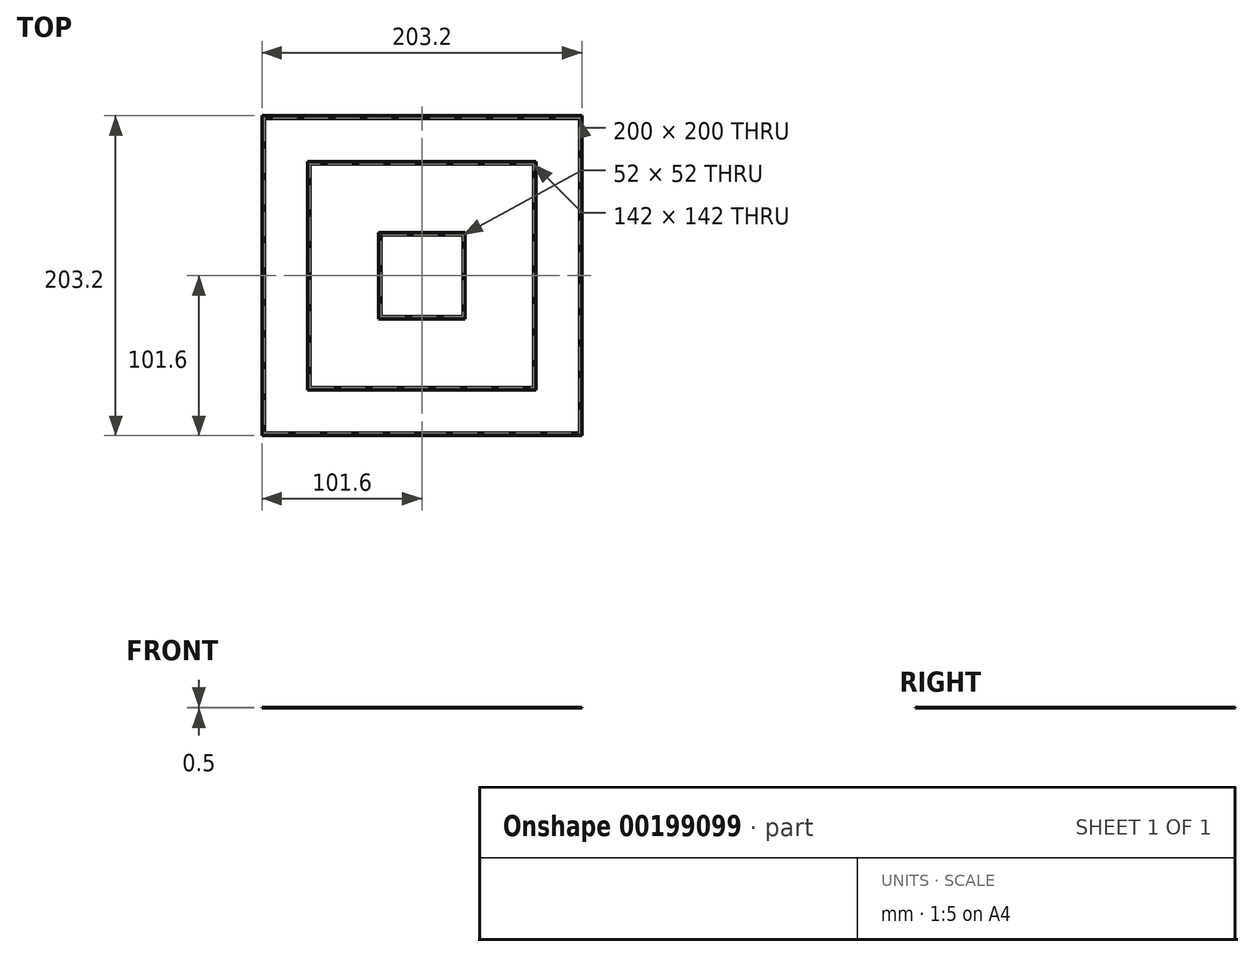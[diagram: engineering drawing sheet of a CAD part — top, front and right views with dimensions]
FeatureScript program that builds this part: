
annotation { "Feature Type Name" : "Feature", "Feature Type Description" : "" }
export const myFeature = defineFeature(function(context is Context, id is Id, definition is map)
    precondition{}
    {
        {
            var Q0;
            Q0=qCreatedBy(makeId("Top.planeOp"),FACE);
            var sketch = newSketch(context, id + "F0", { "sketchPlane" : qUnion([Q0])});
            skLineSegment(sketch, "E0.bottom", {"start": v(101.6, 101.6) * mm, "end": v(-101.6, 101.6) * mm});
            skLineSegment(sketch, "E0.top", {"start": v(101.6, -101.6) * mm, "end": v(-101.6, -101.6) * mm});
            skLineSegment(sketch, "E0.left", {"start": v(101.6, 101.6) * mm, "end": v(101.6, -101.6) * mm});
            skLineSegment(sketch, "E0.right", {"start": v(-101.6, 101.6) * mm, "end": v(-101.6, -101.6) * mm});
            skPoint(sketch, "E0.middle", {"position": v(0, 0) * mm});
            skLineSegment(sketch, "E1.bottom", {"start": v(-100, 100) * mm, "end": v(100, 100) * mm});
            skLineSegment(sketch, "E1.top", {"start": v(-100, -100) * mm, "end": v(100, -100) * mm});
            skLineSegment(sketch, "E1.left", {"start": v(-100, 100) * mm, "end": v(-100, -100) * mm});
            skLineSegment(sketch, "E1.right", {"start": v(100, 100) * mm, "end": v(100, -100) * mm});
            skLineSegment(sketch, "E2.bottom", {"start": v(-27.5, 27.5) * mm, "end": v(27.5, 27.5) * mm});
            skLineSegment(sketch, "E2.top", {"start": v(-27.5, -27.5) * mm, "end": v(27.5, -27.5) * mm});
            skLineSegment(sketch, "E2.left", {"start": v(-27.5, 27.5) * mm, "end": v(-27.5, -27.5) * mm});
            skLineSegment(sketch, "E2.right", {"start": v(27.5, 27.5) * mm, "end": v(27.5, -27.5) * mm});
            skLineSegment(sketch, "E3.bottom", {"start": v(-72.5, 72.5) * mm, "end": v(72.5, 72.5) * mm});
            skLineSegment(sketch, "E3.top", {"start": v(-72.5, -72.5) * mm, "end": v(72.5, -72.5) * mm});
            skLineSegment(sketch, "E3.left", {"start": v(-72.5, 72.5) * mm, "end": v(-72.5, -72.5) * mm});
            skLineSegment(sketch, "E3.right", {"start": v(72.5, 72.5) * mm, "end": v(72.5, -72.5) * mm});
            skLineSegment(sketch, "E4.bottom", {"start": v(-26, 26) * mm, "end": v(26, 26) * mm});
            skLineSegment(sketch, "E4.top", {"start": v(-26, -26) * mm, "end": v(26, -26) * mm});
            skLineSegment(sketch, "E4.left", {"start": v(-26, 26) * mm, "end": v(-26, -26) * mm});
            skLineSegment(sketch, "E4.right", {"start": v(26, 26) * mm, "end": v(26, -26) * mm});
            skLineSegment(sketch, "E5.bottom", {"start": v(-71, 71) * mm, "end": v(71, 71) * mm});
            skLineSegment(sketch, "E5.top", {"start": v(-71, -71) * mm, "end": v(71, -71) * mm});
            skLineSegment(sketch, "E5.left", {"start": v(-71, 71) * mm, "end": v(-71, -71) * mm});
            skLineSegment(sketch, "E5.right", {"start": v(71, 71) * mm, "end": v(71, -71) * mm});
            skSolve(sketch);
        }
        {
            var Q0;
            Q0=makeQuery(id+"F0.imprint","IMPRINT",FACE,{"disambiguationData":[TD([[makeQuery(id+"F0.imprint","IMPRINT",EDGE,{"derivedFrom":sQuery(id+"F0.wireOp",EDGE,"E0.bottom")}),1.0]])]});
            var Q1;
            Q1=makeQuery(id+"F0.imprint","IMPRINT",FACE,{"disambiguationData":[TD([[makeQuery(id+"F0.imprint","IMPRINT",EDGE,{"derivedFrom":sQuery(id+"F0.wireOp",EDGE,"E2.bottom")}),-1.0]])]});
            var Q2;
            Q2=makeQuery(id+"F0.imprint","IMPRINT",FACE,{"disambiguationData":[TD([[makeQuery(id+"F0.imprint","IMPRINT",EDGE,{"derivedFrom":sQuery(id+"F0.wireOp",EDGE,"E3.bottom")}),-1.0]])]});
            extrude(context, id + "F1", {"entities" : qUnion([Q0, Q1, Q2]), "depth" : .5 * mm});
        }
    });
